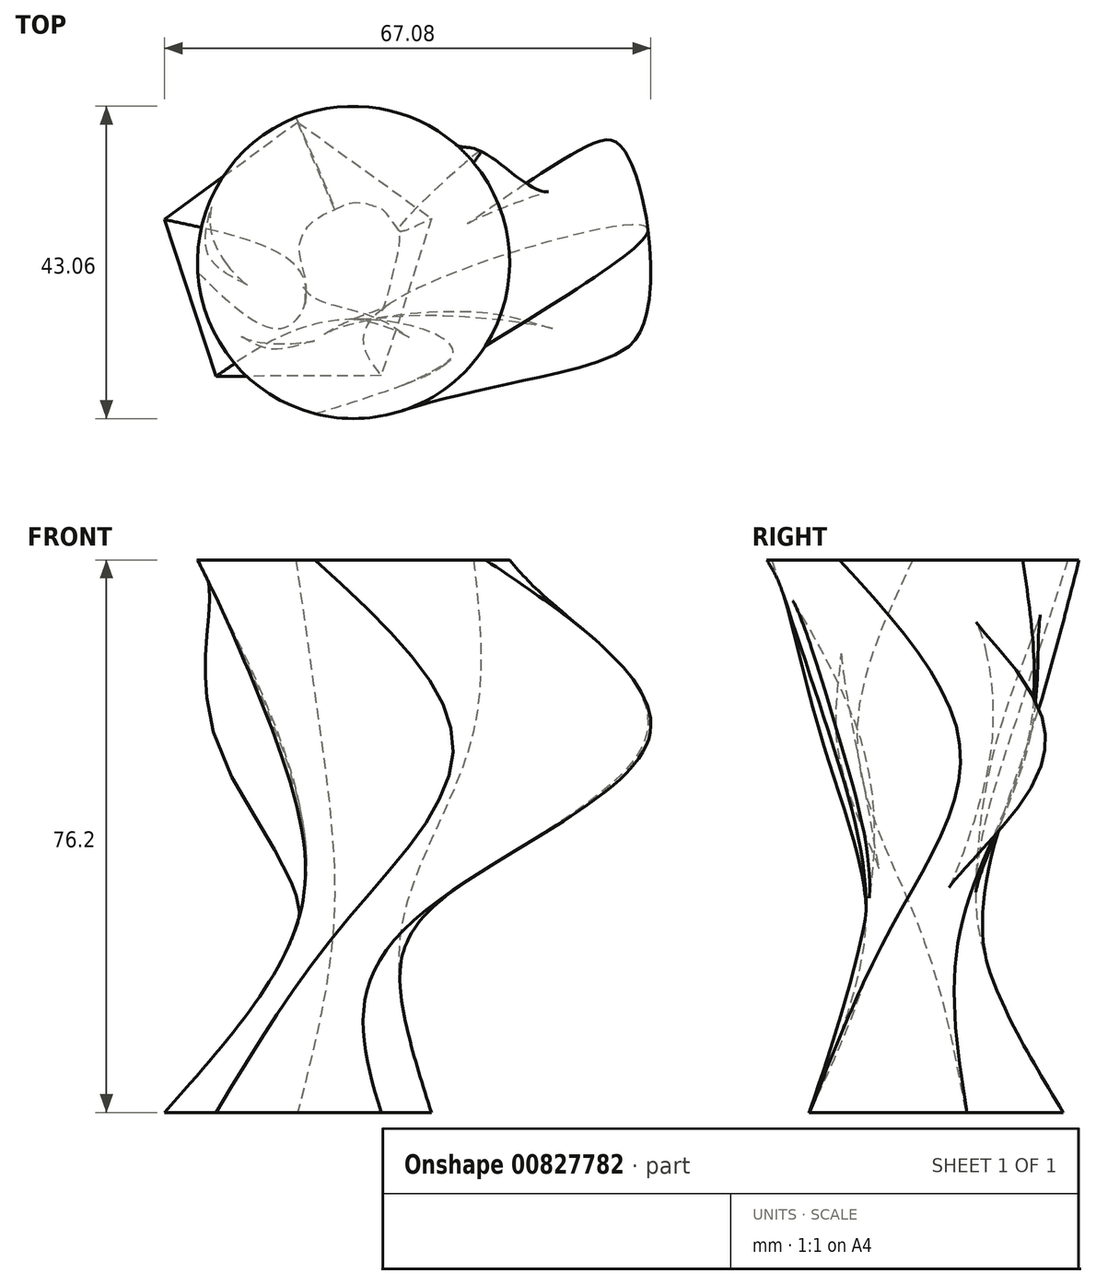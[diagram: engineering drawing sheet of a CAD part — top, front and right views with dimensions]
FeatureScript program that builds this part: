
annotation { "Feature Type Name" : "Feature", "Feature Type Description" : "" }
export const myFeature = defineFeature(function(context is Context, id is Id, definition is map)
    precondition{}
    {
        {
            var Q0;
            Q0=qCreatedBy(makeId("Top.planeOp"),FACE);
            cPlane(context, id + "F0", {"entities" : qUnion([Q0]), "cplaneType" : CPlaneType.OFFSET, "offset" : 25.4 * mm, "width" : 152.4 * mm, "height" : 152.4 * mm});
        }
        {
            var Q0;
            Q0=qCreatedBy(id+"F0.planeOp",FACE);
            cPlane(context, id + "F1", {"entities" : qUnion([Q0]), "cplaneType" : CPlaneType.OFFSET, "offset" : 25.4 * mm, "width" : 152.4 * mm, "height" : 152.4 * mm});
        }
        {
            var Q0;
            Q0=qCreatedBy(id+"F1.planeOp",FACE);
            cPlane(context, id + "F2", {"entities" : qUnion([Q0]), "cplaneType" : CPlaneType.OFFSET, "offset" : 25.4 * mm, "width" : 152.4 * mm, "height" : 152.4 * mm});
        }
        {
            var Q0;
            Q0=qCreatedBy(makeId("Top.planeOp"),FACE);
            var sketch = newSketch(context, id + "F3", { "sketchPlane" : qUnion([Q0])});
            skCircle(sketch, "E0.cCircle", {"center": v(0, 0) * mm, "radius": 15.67 * mm, "construction": true});
            skLineSegment(sketch, "E0.0", {"start": v(-0.08, 19.37) * mm, "end": v(18.4, 6.06) * mm});
            skLineSegment(sketch, "E0.1", {"start": v(18.4, 6.06) * mm, "end": v(11.45, -15.62) * mm});
            skLineSegment(sketch, "E0.2", {"start": v(11.45, -15.62) * mm, "end": v(-11.32, -15.71) * mm});
            skLineSegment(sketch, "E0.3", {"start": v(-11.32, -15.71) * mm, "end": v(-18.44, 5.9) * mm});
            skLineSegment(sketch, "E0.4", {"start": v(-18.44, 5.9) * mm, "end": v(-0.08, 19.37) * mm});
            skPoint(sketch, "E0.0.midPoint", {"position": v(9.16, 12.71) * mm});
            skSolve(sketch);
        }
        {
            var Q0;
            Q0=qCreatedBy(id+"F0.planeOp",FACE);
            var sketch = newSketch(context, id + "F4", { "sketchPlane" : qUnion([Q0])});
            skCircle(sketch, "E1", {"center": v(7.85, 0) * mm, "radius": 8.21 * mm});
            skSolve(sketch);
        }
        {
            var Q0;
            Q0=qCreatedBy(id+"F1.planeOp",FACE);
            var sketch = newSketch(context, id + "F5", { "sketchPlane" : qUnion([Q0])});
            skFitSpline(sketch, "E2", {"points": [v(0, 10.25) * mm, v(7.87, 14.02) * mm, v(8.35, 14.4) * mm, v(14.6, 10.08) * mm, v(22.44, 14.56) * mm, v(34.01, 9.61) * mm, v(42.97, 16.82) * mm, v(46.05, -9.91) * mm, v(27.86, -8.5) * mm, v(19.05, -13.73) * mm, v(10.53, -9.35) * mm, v(-2.7, -11.6) * mm, v(-2.46, -6.25) * mm, v(-11.08, 0) * mm, v(0, 10.25) * mm]});
            skSolve(sketch);
        }
        {
            var Q0;
            Q0=qCreatedBy(id+"F2.planeOp",FACE);
            var sketch = newSketch(context, id + "F6", { "sketchPlane" : qUnion([Q0])});
            skCircle(sketch, "E3", {"center": v(7.64, 0) * mm, "radius": 21.53 * mm});
            skSolve(sketch);
        }
        {
            var Q0;
            Q0 = qSketchRegion(id + "F6", true);
            var Q1;
            Q1 = qSketchRegion(id + "F5", true);
            var Q2;
            Q2 = qSketchRegion(id + "F4", true);
            var Q3;
            Q3 = qSketchRegion(id + "F3", true);
            loft(context, id + "F7", {"sheetProfilesArray" : [{ "sheetProfileEntities" : qUnion([Q0]) }, { "sheetProfileEntities" : qUnion([Q1]) }, { "sheetProfileEntities" : qUnion([Q2]) }, { "sheetProfileEntities" : qUnion([Q3]) }]});
        }
    });
